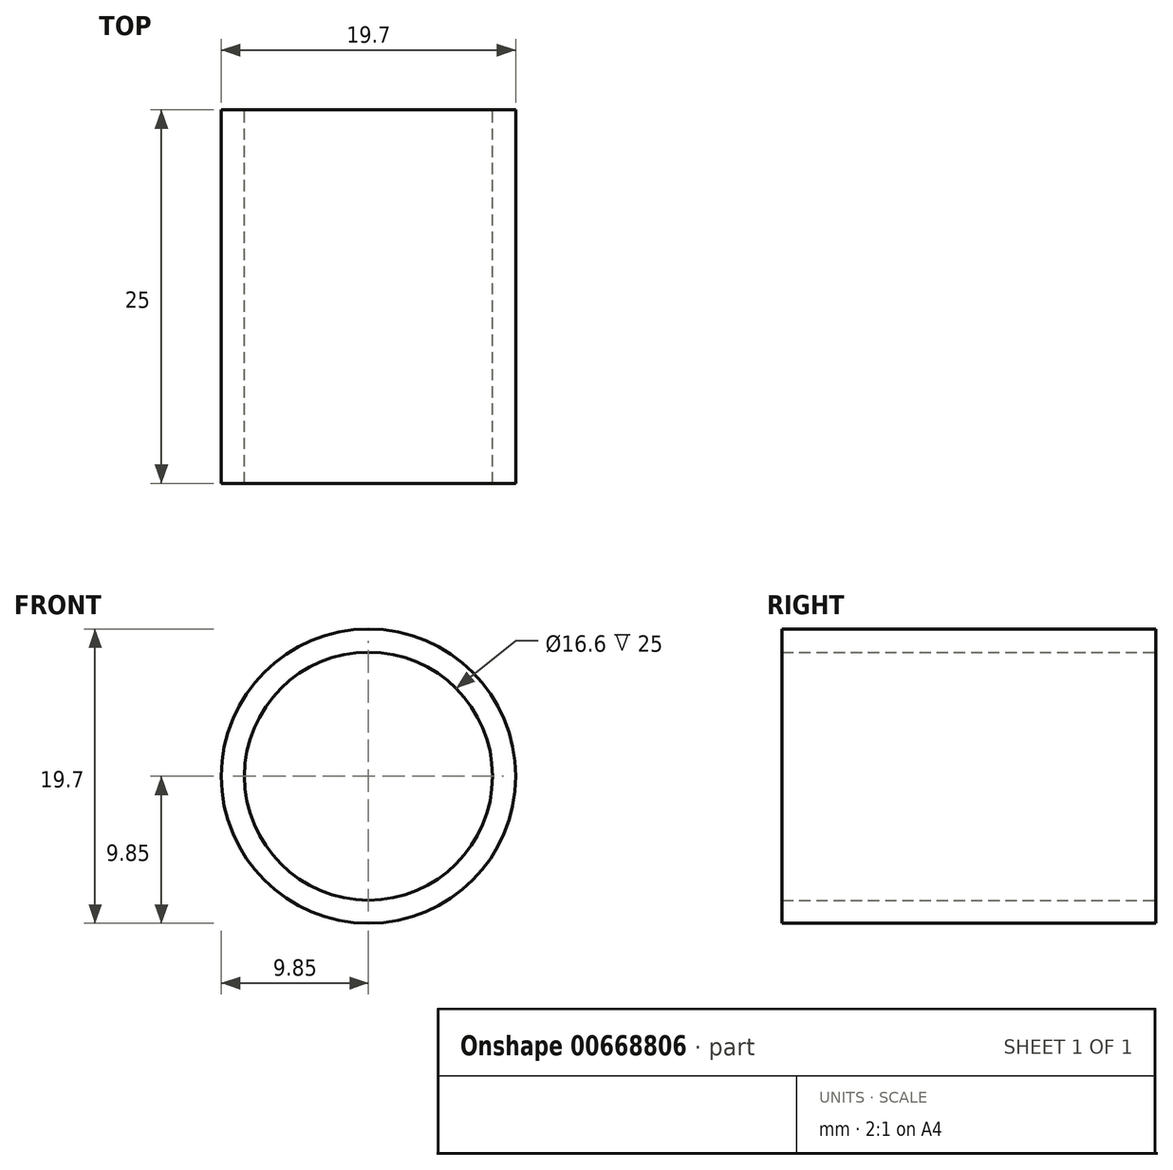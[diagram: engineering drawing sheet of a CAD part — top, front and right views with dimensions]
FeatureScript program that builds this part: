
annotation { "Feature Type Name" : "Feature", "Feature Type Description" : "" }
export const myFeature = defineFeature(function(context is Context, id is Id, definition is map)
    precondition{}
    {
        {
            var Q0;
            Q0=qCreatedBy(makeId("Front.planeOp"),FACE);
            var sketch = newSketch(context, id + "F0", { "sketchPlane" : qUnion([Q0])});
            skCircle(sketch, "E0", {"center": v(0, 0) * mm, "radius": 9.85 * mm});
            skCircle(sketch, "E1", {"center": v(0, 0) * mm, "radius": 8.3 * mm});
            skSolve(sketch);
        }
        {
            var Q0;
            Q0 = qSketchRegion(id + "F0", true);
            var Q1;
            Q1=sQuery(id+"F0.wireOp",EDGE,"E0");
            var Q2;
            Q2=sQuery(id+"F0.wireOp",EDGE,"E1");
            extrude(context, id + "F1", {"bodyType" : ToolBodyType.SURFACE, "surfaceEntities" : qUnion([Q0, Q1, Q2]), "depth" : 25 * mm, "offsetDistance" : 25 * mm});
        }
    });
